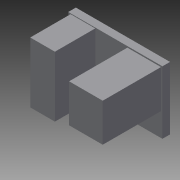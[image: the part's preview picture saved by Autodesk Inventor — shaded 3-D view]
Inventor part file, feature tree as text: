
AUTODESK INVENTOR PART (.ipt)
format: ipt  version: 2013 SP2 (Build 170200200, 200)  size: 99,840 bytes
history: native  units: mm
features: extrude x3, sketch x3
ambient origin geometry x8: Origin, YZ Plane, XZ Plane, XY Plane, X Axis, Y Axis, Z Axis, Center Point
bodies: Solid1 (feature_tree)
feature tree (6):
  extrude  "Extrusion1"  Depth=14.0mm
  extrude  "Extrusion2"  Depth=20.0mm
  extrude  "Extrusion3"  Depth=13.5mm
  sketch  "Sketch1"  dims[d0=21.0mm d1=14.0mm]
  sketch  "Sketch2"  dims[d2=1.7mm d3=0.0mm d10=20.0mm d12=2.54mm d13=50.0mm d15=2.54mm]
  sketch  "Sketch3"  dims[d18=5.5mm d19=13.5mm d20=4.38mm d21=4.54mm d22=9.0mm d23=0.0mm d25=19.1mm d26=3.5mm d27=7.5mm d28=8.5mm d31=13.0mm d32=0.0mm]
